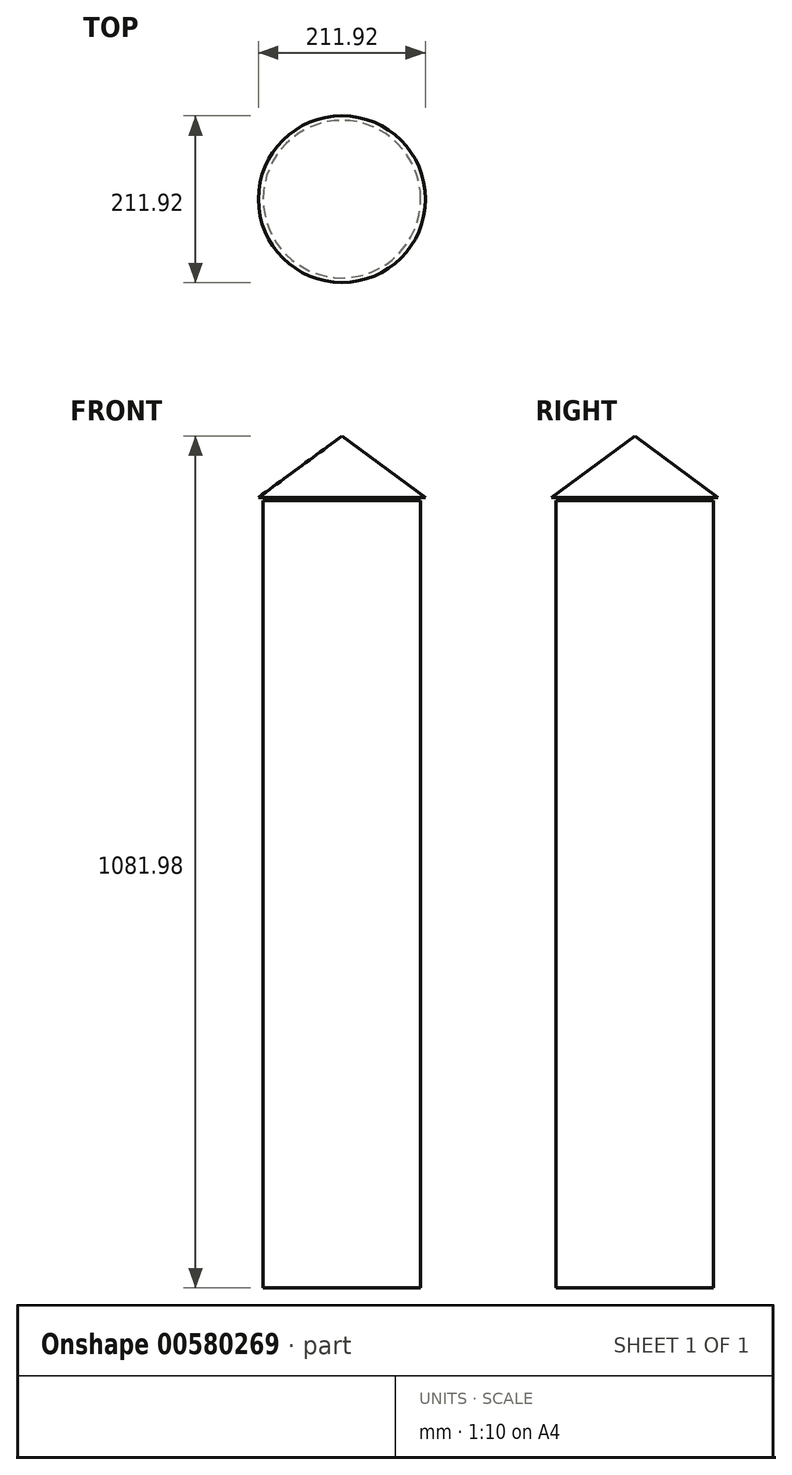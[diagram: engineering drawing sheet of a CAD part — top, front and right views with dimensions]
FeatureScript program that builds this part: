
annotation { "Feature Type Name" : "Feature", "Feature Type Description" : "" }
export const myFeature = defineFeature(function(context is Context, id is Id, definition is map)
    precondition{}
    {
        {
            var Q0;
            Q0=qCreatedBy(makeId("Top.planeOp"),FACE);
            var sketch = newSketch(context, id + "F0", { "sketchPlane" : qUnion([Q0])});
            skCircle(sketch, "E0", {"center": v(0, 0) * mm, "radius": 100 * mm});
            skSolve(sketch);
        }
        {
            var Q0;
            Q0 = qSketchRegion(id + "F0", true);
            extrude(context, id + "F1", {"entities" : qUnion([Q0]), "depth" : 1000 * mm, "offsetDistance" : 25 * mm});
        }
        {
            var Q0;
            Q0=qCreatedBy(makeId("Right.planeOp"),FACE);
            var sketch = newSketch(context, id + "F2", { "sketchPlane" : qUnion([Q0])});
            skLineSegment(sketch, "E1", {"start": v(0, 1004.04) * mm, "end": v(0, 1081.98) * mm});
            skLineSegment(sketch, "E2", {"start": v(0, 1081.98) * mm, "end": v(-105.96, 1004.04) * mm});
            skLineSegment(sketch, "E3", {"start": v(-105.96, 1004.04) * mm, "end": v(0, 1004.04) * mm});
            skSolve(sketch);
        }
        {
            var Q0;
            Q0=makeQuery(id+"F2.imprint","IMPRINT",FACE,{"disambiguationData":[TD([[makeQuery(id+"F2.imprint","IMPRINT",EDGE,{"derivedFrom":sQuery(id+"F2.wireOp",EDGE,"E1")}),1.0]])]});
            var Q1;
            Q1=sQuery(id+"F2.wireOp",EDGE,"E1");
            revolve(context, id + "F3", {"entities" : qUnion([Q0]), "axis" : qUnion([Q1]), "revolveType" : RevolveType.FULL});
        }
    });
